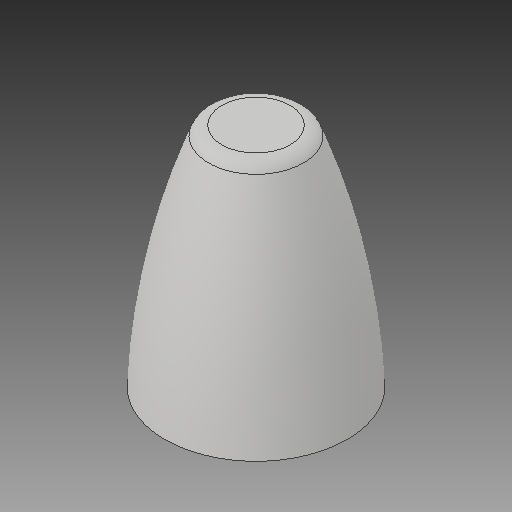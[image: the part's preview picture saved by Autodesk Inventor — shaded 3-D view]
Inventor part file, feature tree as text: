
AUTODESK INVENTOR PART (.ipt)
format: ipt  version: 2018 (Build 220112000, 112)  size: 166,400 bytes
history: native  units: in
note: dims shown in document units (in); Inventor stores cm internally (conversion verified against a paired STEP export)
features: fillet x1
ambient origin geometry x8: Origin, YZ Plane, XZ Plane, XY Plane, X Axis, Y Axis, Z Axis, Center Point
bodies: Solid1 (feature_tree)
feature tree (1):
  fillet  "Fillet3"  [1 undecoded]
note: 1 required parameter value undecoded (feature->parameter linkage not recoverable at this tier; creation-order binding heuristic only, values carry confidence <= 0.55)
